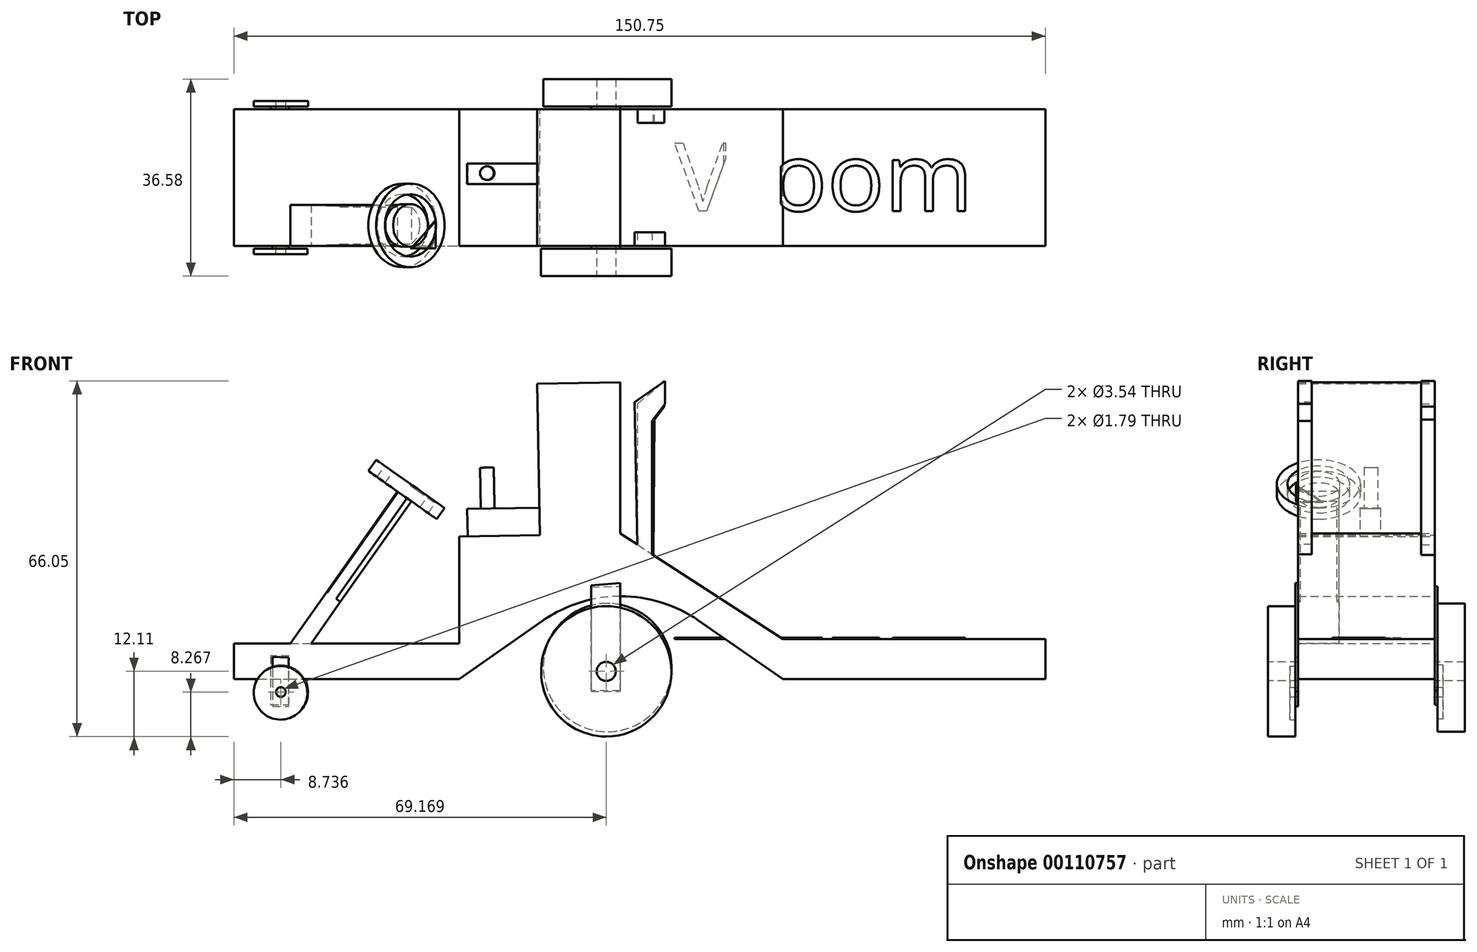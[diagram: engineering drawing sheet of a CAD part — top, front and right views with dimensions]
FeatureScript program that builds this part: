
annotation { "Feature Type Name" : "Feature", "Feature Type Description" : "" }
export const myFeature = defineFeature(function(context is Context, id is Id, definition is map)
    precondition{}
    {
        {
            var Q0;
            Q0=qCreatedBy(makeId("Front.planeOp"),FACE);
            var sketch = newSketch(context, id + "F0", { "sketchPlane" : qUnion([Q0])});
            skLineSegment(sketch, "E0", {"start": v(-71.8, 16.69) * mm, "end": v(-29.94, 16.69) * mm});
            skLineSegment(sketch, "E1", {"start": v(-29.94, 16.69) * mm, "end": v(-14.49, 27.49) * mm});
            skLineSegment(sketch, "E2", {"start": v(14.53, 27.55) * mm, "end": v(30.2, 16.69) * mm});
            skLineSegment(sketch, "E3", {"start": v(30.2, 16.69) * mm, "end": v(78.95, 16.69) * mm});
            skArc(sketch, "E4.filletArc", {"start": v(14.53, 27.55) * mm, "mid": v(0.01, 32.07) * mm, "end": v(-14.49, 27.49) * mm});
            skLineSegment(sketch, "E5", {"start": v(-71.8, 16.69) * mm, "end": v(-71.8, 23.31) * mm});
            skLineSegment(sketch, "E6", {"start": v(-71.8, 23.31) * mm, "end": v(-29.94, 23.31) * mm});
            skLineSegment(sketch, "E7", {"start": v(-29.94, 23.31) * mm, "end": v(0, 43.71) * mm});
            skLineSegment(sketch, "E8", {"start": v(0, 43.71) * mm, "end": v(30.2, 24.1) * mm});
            skLineSegment(sketch, "E9", {"start": v(30.2, 24.1) * mm, "end": v(78.95, 24.1) * mm});
            skLineSegment(sketch, "E10", {"start": v(78.95, 24.1) * mm, "end": v(78.95, 16.69) * mm});
            skLineSegment(sketch, "E11", {"start": v(-29.94, 23.31) * mm, "end": v(-29.94, 43.18) * mm});
            skLineSegment(sketch, "E12", {"start": v(-29.94, 43.18) * mm, "end": v(0, 43.71) * mm});
            skLineSegment(sketch, "E13", {"start": v(-14.97, 43.45) * mm, "end": v(-15.47, 71.53) * mm});
            skLineSegment(sketch, "E14", {"start": v(-15.47, 71.53) * mm, "end": v(0, 71.8) * mm});
            skLineSegment(sketch, "E15", {"start": v(0, 71.8) * mm, "end": v(0, 43.71) * mm});
            skSolve(sketch);
        }
        {
            var Q0;
            Q0 = qSketchRegion(id + "F0", true);
            extrude(context, id + "F1", {"entities" : qUnion([Q0]), "depth" : 25.4 * mm});
        }
        {
            var Q0;
            Q0=makeQuery(id+"F1.opExtrude","CAP_FACE",FACE,{"disambiguationData":[OSD([sQuery(id+"F0.wireOp",EDGE,"E0"),sQuery(id+"F0.wireOp",EDGE,"E1"),sQuery(id+"F0.wireOp",EDGE,"E2"),sQuery(id+"F0.wireOp",EDGE,"E3"),sQuery(id+"F0.wireOp",EDGE,"E4.filletArc"),sQuery(id+"F0.wireOp",EDGE,"E5"),sQuery(id+"F0.wireOp",EDGE,"E6"),sQuery(id+"F0.wireOp",EDGE,"E8"),sQuery(id+"F0.wireOp",EDGE,"E9"),sQuery(id+"F0.wireOp",EDGE,"E10"),sQuery(id+"F0.wireOp",EDGE,"E11"),sQuery(id+"F0.wireOp",EDGE,"E12"),sQuery(id+"F0.wireOp",EDGE,"E13"),sQuery(id+"F0.wireOp",EDGE,"E14"),sQuery(id+"F0.wireOp",EDGE,"E15")])],"isStart":false});
            var sketch = newSketch(context, id + "F2", { "sketchPlane" : qUnion([Q0])});
            skLineSegment(sketch, "E16", {"start": v(-5.44, 34.07) * mm, "end": v(-5.44, 31.47) * mm});
            skLineSegment(sketch, "E17", {"start": v(-5.44, 31.47) * mm, "end": v(-5.44, 14.38) * mm});
            skLineSegment(sketch, "E18", {"start": v(-5.44, 14.38) * mm, "end": v(0, 14.38) * mm});
            skLineSegment(sketch, "E19", {"start": v(0, 14.38) * mm, "end": v(0, 34.55) * mm});
            skLineSegment(sketch, "E20", {"start": v(0, 34.55) * mm, "end": v(-5.44, 34.07) * mm});
            skSolve(sketch);
        }
        {
            var Q0;
            Q0 = qSketchRegion(id + "F2", true);
            extrude(context, id + "F3", {"entities" : qUnion([Q0]), "operationType" : NewBodyOperationType.ADD, "depth" : 0.5 * mm});
        }
        {
            var Q0;
            Q0=makeQuery(id+"F1.opExtrude","CAP_FACE",FACE,{"disambiguationData":[OSD([sQuery(id+"F0.wireOp",EDGE,"E0"),sQuery(id+"F0.wireOp",EDGE,"E1"),sQuery(id+"F0.wireOp",EDGE,"E2"),sQuery(id+"F0.wireOp",EDGE,"E3"),sQuery(id+"F0.wireOp",EDGE,"E4.filletArc"),sQuery(id+"F0.wireOp",EDGE,"E5"),sQuery(id+"F0.wireOp",EDGE,"E6"),sQuery(id+"F0.wireOp",EDGE,"E8"),sQuery(id+"F0.wireOp",EDGE,"E9"),sQuery(id+"F0.wireOp",EDGE,"E10"),sQuery(id+"F0.wireOp",EDGE,"E11"),sQuery(id+"F0.wireOp",EDGE,"E12"),sQuery(id+"F0.wireOp",EDGE,"E13"),sQuery(id+"F0.wireOp",EDGE,"E14"),sQuery(id+"F0.wireOp",EDGE,"E15")])],"isStart":true});
            var sketch = newSketch(context, id + "F4", { "sketchPlane" : qUnion([Q0])});
            skLineSegment(sketch, "E21", {"start": v(0, 33.92) * mm, "end": v(0, 14.54) * mm});
            skLineSegment(sketch, "E22", {"start": v(0, 14.54) * mm, "end": v(5.42, 14.54) * mm});
            skLineSegment(sketch, "E23", {"start": v(5.42, 14.54) * mm, "end": v(5.42, 33.76) * mm});
            skLineSegment(sketch, "E24", {"start": v(5.42, 33.76) * mm, "end": v(0, 33.92) * mm});
            skSolve(sketch);
        }
        {
            var Q0;
            Q0 = qSketchRegion(id + "F4", true);
            extrude(context, id + "F5", {"entities" : qUnion([Q0]), "operationType" : NewBodyOperationType.ADD, "depth" : 0.5 * mm});
        }
        {
            var Q0;
            Q0=makeQuery(id+"F3.opExtrude","CAP_FACE",FACE,{"disambiguationData":[OSD([sQuery(id+"F2.wireOp",EDGE,"E16"),sQuery(id+"F2.wireOp",EDGE,"E17"),sQuery(id+"F2.wireOp",EDGE,"E18"),sQuery(id+"F2.wireOp",EDGE,"E19"),sQuery(id+"F2.wireOp",EDGE,"E20")])],"isStart":false});
            var sketch = newSketch(context, id + "F6", { "sketchPlane" : qUnion([Q0])});
            skCircle(sketch, "E25", {"center": v(-2.63, 18.12) * mm, "radius": 12.1 * mm});
            skSolve(sketch);
        }
        {
            var Q0;
            Q0 = qSketchRegion(id + "F6", true);
            extrude(context, id + "F7", {"entities" : qUnion([Q0]), "operationType" : NewBodyOperationType.ADD, "depth" : 5.08 * mm});
        }
        {
            var Q0;
            Q0=makeQuery(id+"F5.opExtrude","CAP_FACE",FACE,{"disambiguationData":[OSD([sQuery(id+"F4.wireOp",EDGE,"E21"),sQuery(id+"F4.wireOp",EDGE,"E22"),sQuery(id+"F4.wireOp",EDGE,"E23"),sQuery(id+"F4.wireOp",EDGE,"E24")])],"isStart":false});
            var sketch = newSketch(context, id + "F8", { "sketchPlane" : qUnion([Q0])});
            skCircle(sketch, "E26", {"center": v(2.4, 18.83) * mm, "radius": 11.92 * mm});
            skSolve(sketch);
        }
        {
            var Q0;
            Q0 = qSketchRegion(id + "F8", true);
            extrude(context, id + "F9", {"entities" : qUnion([Q0]), "operationType" : NewBodyOperationType.ADD, "depth" : 5.08 * mm});
        }
        {
            var Q0;
            Q0=makeQuery(id+"F1.opExtrude","CAP_FACE",FACE,{"disambiguationData":[OSD([sQuery(id+"F0.wireOp",EDGE,"E0"),sQuery(id+"F0.wireOp",EDGE,"E1"),sQuery(id+"F0.wireOp",EDGE,"E2"),sQuery(id+"F0.wireOp",EDGE,"E3"),sQuery(id+"F0.wireOp",EDGE,"E4.filletArc"),sQuery(id+"F0.wireOp",EDGE,"E5"),sQuery(id+"F0.wireOp",EDGE,"E6"),sQuery(id+"F0.wireOp",EDGE,"E8"),sQuery(id+"F0.wireOp",EDGE,"E9"),sQuery(id+"F0.wireOp",EDGE,"E10"),sQuery(id+"F0.wireOp",EDGE,"E11"),sQuery(id+"F0.wireOp",EDGE,"E12"),sQuery(id+"F0.wireOp",EDGE,"E13"),sQuery(id+"F0.wireOp",EDGE,"E14"),sQuery(id+"F0.wireOp",EDGE,"E15")])],"isStart":false});
            var sketch = newSketch(context, id + "F10", { "sketchPlane" : qUnion([Q0])});
            skLineSegment(sketch, "E27", {"start": v(-61.3, 23.31) * mm, "end": v(-41.43, 51.53) * mm});
            skLineSegment(sketch, "E28", {"start": v(-41.43, 51.53) * mm, "end": v(-38.85, 49.72) * mm});
            skLineSegment(sketch, "E29", {"start": v(-38.85, 49.72) * mm, "end": v(-57.45, 23.31) * mm});
            skLineSegment(sketch, "E30", {"start": v(-57.45, 23.31) * mm, "end": v(-61.3, 23.31) * mm});
            skSolve(sketch);
        }
        {
            var Q0;
            Q0 = qSketchRegion(id + "F10", true);
            extrude(context, id + "F11", {"entities" : qUnion([Q0]), "operationType" : NewBodyOperationType.ADD, "oppositeDirection" : true, "depth" : 7.62 * mm});
        }
        {
            var Q0;
            Q0=makeQuery(id+"F11.opExtrude","SWEPT_FACE",FACE,{"disambiguationData":[OSD([sQuery(id+"F10.wireOp",EDGE,"E28")])]});
            var sketch = newSketch(context, id + "F12", { "sketchPlane" : qUnion([Q0])});
            skCircle(sketch, "E31", {"center": v(-62.38, -21.6) * mm, "radius": 7.77 * mm});
            skPoint(sketch, "E31.centerSnap0", {"position": v(-60.4, -21.6) * mm});
            skSolve(sketch);
        }
        {
            var Q0;
            Q0 = qSketchRegion(id + "F12", true);
            extrude(context, id + "F13", {"entities" : qUnion([Q0]), "operationType" : NewBodyOperationType.ADD, "depth" : 2.54 * mm});
        }
        {
            var Q0;
            Q0=makeQuery(id+"F13.opExtrude","CAP_FACE",FACE,{"disambiguationData":[OSD([sQuery(id+"F12.wireOp",EDGE,"E31")])],"isStart":false});
            var sketch = newSketch(context, id + "F14", { "sketchPlane" : qUnion([Q0])});
            skCircle(sketch, "E32", {"center": v(-62.38, -21.6) * mm, "radius": 5.78 * mm});
            skCircle(sketch, "E33", {"center": v(-62.38, -21.6) * mm, "radius": 3.94 * mm});
            skSolve(sketch);
        }
        {
            var Q0;
            Q0 = qSketchRegion(id + "F14", true);
            extrude(context, id + "F15", {"entities" : qUnion([Q0]), "operationType" : NewBodyOperationType.REMOVE, "oppositeDirection" : true, "depth" : 25.4 * mm});
        }
        {
            var Q0;
            {var subQ0=sQuery(id+"F12.wireOp",EDGE,"E31");Q0=makeQuery(id+"F15.boolean.opBoolean","SPLIT",FACE,{"disambiguationData":[TD([makeQuery(id+"F13.opExtrude","SWEPT_FACE",FACE,{"disambiguationData":[OSD([subQ0])]})])],"derivedFrom":makeQuery(id+"F13.opExtrude","CAP_FACE",FACE,{"disambiguationData":[OSD([subQ0])],"isStart":false})});}
            var sketch = newSketch(context, id + "F16", { "sketchPlane" : qUnion([Q0])});
            skLineSegment(sketch, "E34", {"start": v(-63.82, -27.19) * mm, "end": v(-60.63, -24.46) * mm});
            skLineSegment(sketch, "E35", {"start": v(-60.63, -24.46) * mm, "end": v(-56.65, -20.78) * mm});
            skLineSegment(sketch, "E36", {"start": v(-56.65, -20.78) * mm, "end": v(-56.65, -25.82) * mm});
            skPoint(sketch, "E36.endSnap0", {"position": v(-62.22, -25.82) * mm});
            skLineSegment(sketch, "E37", {"start": v(-56.65, -25.82) * mm, "end": v(-62.22, -25.82) * mm});
            skSolve(sketch);
        }
        {
            var Q0;
            Q0 = qSketchRegion(id + "F16", true);
            extrude(context, id + "F17", {"entities" : qUnion([Q0]), "oppositeDirection" : true, "depth" : 0.25 * mm});
        }
        {
            var Q0;
            Q0=makeQuery(id+"F1.opExtrude","SWEPT_FACE",FACE,{"disambiguationData":[OSD([sQuery(id+"F0.wireOp",EDGE,"E9")])]});
            var sketch = newSketch(context, id + "F18", { "sketchPlane" : qUnion([Q0])});
            skText(sketch, "E38", { "text": "Vroom", "fontName": "OpenSans-Regular.ttf"});
            const initialGuessF18  = {"E38": [0.01007, -0.0189, 1, 0, 0.0127]};
            skSetInitialGuess(sketch, initialGuessF18);
            skSolve(sketch);
        }
        {
            var Q0;
            Q0 = qSketchRegion(id + "F18", true);
            extrude(context, id + "F19", {"entities" : qUnion([Q0]), "operationType" : NewBodyOperationType.ADD, "depth" : 0.25 * mm});
        }
        {
            var Q0;
            Q0=makeQuery(id+"F11.boolean.opBoolean","MERGE",FACE,{"derivedFrom":[makeQuery(id+"F1.opExtrude","CAP_FACE",FACE,{"disambiguationData":[OSD([sQuery(id+"F0.wireOp",EDGE,"E0"),sQuery(id+"F0.wireOp",EDGE,"E1"),sQuery(id+"F0.wireOp",EDGE,"E2"),sQuery(id+"F0.wireOp",EDGE,"E3"),sQuery(id+"F0.wireOp",EDGE,"E4.filletArc"),sQuery(id+"F0.wireOp",EDGE,"E5"),sQuery(id+"F0.wireOp",EDGE,"E6"),sQuery(id+"F0.wireOp",EDGE,"E8"),sQuery(id+"F0.wireOp",EDGE,"E9"),sQuery(id+"F0.wireOp",EDGE,"E10"),sQuery(id+"F0.wireOp",EDGE,"E11"),sQuery(id+"F0.wireOp",EDGE,"E12"),sQuery(id+"F0.wireOp",EDGE,"E13"),sQuery(id+"F0.wireOp",EDGE,"E14"),sQuery(id+"F0.wireOp",EDGE,"E15")])],"isStart":false}),makeQuery(id+"F11.opExtrude","CAP_FACE",FACE,{"disambiguationData":[OSD([sQuery(id+"F10.wireOp",EDGE,"E27"),sQuery(id+"F10.wireOp",EDGE,"E28"),sQuery(id+"F10.wireOp",EDGE,"E29"),sQuery(id+"F10.wireOp",EDGE,"E30")])],"isStart":true})]});
            var sketch = newSketch(context, id + "F20", { "sketchPlane" : qUnion([Q0])});
            skLineSegment(sketch, "E39", {"start": v(3.12, 41.69) * mm, "end": v(2.65, 68.1) * mm});
            skLineSegment(sketch, "E40", {"start": v(2.65, 68.1) * mm, "end": v(8.26, 72.06) * mm});
            skLineSegment(sketch, "E41", {"start": v(8.26, 72.06) * mm, "end": v(8.26, 67.82) * mm});
            skLineSegment(sketch, "E42", {"start": v(8.26, 67.82) * mm, "end": v(5.88, 64.64) * mm});
            skLineSegment(sketch, "E43", {"start": v(5.88, 64.64) * mm, "end": v(5.88, 39.9) * mm});
            skLineSegment(sketch, "E44", {"start": v(5.88, 39.9) * mm, "end": v(3.12, 41.69) * mm});
            skSolve(sketch);
        }
        {
            var Q0;
            Q0=makeQuery(id+"F1.opExtrude","CAP_FACE",FACE,{"disambiguationData":[OSD([sQuery(id+"F0.wireOp",EDGE,"E0"),sQuery(id+"F0.wireOp",EDGE,"E1"),sQuery(id+"F0.wireOp",EDGE,"E2"),sQuery(id+"F0.wireOp",EDGE,"E3"),sQuery(id+"F0.wireOp",EDGE,"E4.filletArc"),sQuery(id+"F0.wireOp",EDGE,"E5"),sQuery(id+"F0.wireOp",EDGE,"E6"),sQuery(id+"F0.wireOp",EDGE,"E8"),sQuery(id+"F0.wireOp",EDGE,"E9"),sQuery(id+"F0.wireOp",EDGE,"E10"),sQuery(id+"F0.wireOp",EDGE,"E11"),sQuery(id+"F0.wireOp",EDGE,"E12"),sQuery(id+"F0.wireOp",EDGE,"E13"),sQuery(id+"F0.wireOp",EDGE,"E14"),sQuery(id+"F0.wireOp",EDGE,"E15")])],"isStart":true});
            var sketch = newSketch(context, id + "F21", { "sketchPlane" : qUnion([Q0])});
            skLineSegment(sketch, "E45", {"start": v(-6.13, 39.73) * mm, "end": v(-3.23, 41.61) * mm});
            skLineSegment(sketch, "E46", {"start": v(-3.23, 41.61) * mm, "end": v(-3.23, 67.82) * mm});
            skLineSegment(sketch, "E47", {"start": v(-3.23, 67.82) * mm, "end": v(-8.16, 72.06) * mm});
            skLineSegment(sketch, "E48", {"start": v(-8.16, 72.06) * mm, "end": v(-8.16, 67.3) * mm});
            skLineSegment(sketch, "E49", {"start": v(-8.16, 67.3) * mm, "end": v(-6.3, 64.9) * mm});
            skLineSegment(sketch, "E50", {"start": v(-6.3, 64.9) * mm, "end": v(-6.13, 39.73) * mm});
            skSolve(sketch);
        }
        {
            var Q0;
            Q0 = qSketchRegion(id + "F21", true);
            extrude(context, id + "F22", {"entities" : qUnion([Q0]), "operationType" : NewBodyOperationType.ADD, "oppositeDirection" : true, "depth" : 2.54 * mm});
        }
        {
            var Q0;
            Q0 = qSketchRegion(id + "F20", true);
            extrude(context, id + "F23", {"entities" : qUnion([Q0]), "operationType" : NewBodyOperationType.ADD, "oppositeDirection" : true, "depth" : 2.54 * mm});
        }
        {
            var Q0;
            Q0=makeQuery(id+"F1.opExtrude","SWEPT_FACE",FACE,{"disambiguationData":[OSD([sQuery(id+"F0.wireOp",EDGE,"E12")])]});
            var sketch = newSketch(context, id + "F24", { "sketchPlane" : qUnion([Q0])});
            skLineSegment(sketch, "E51", {"start": v(-14.2, -10.09) * mm, "end": v(-22.53, -10.09) * mm});
            skLineSegment(sketch, "E52", {"start": v(-22.53, -13.93) * mm, "end": v(-14.2, -13.93) * mm});
            skLineSegment(sketch, "E53", {"start": v(-14.2, -13.93) * mm, "end": v(-14.2, -10.09) * mm});
            skLineSegment(sketch, "E54", {"start": v(-22.53, -10.09) * mm, "end": v(-27.6, -10.09) * mm});
            skLineSegment(sketch, "E55", {"start": v(-27.6, -10.09) * mm, "end": v(-27.6, -13.93) * mm});
            skLineSegment(sketch, "E56", {"start": v(-27.6, -13.93) * mm, "end": v(-22.53, -13.93) * mm});
            skSolve(sketch);
        }
        {
            var Q0;
            Q0 = qSketchRegion(id + "F24", true);
            extrude(context, id + "F25", {"entities" : qUnion([Q0]), "operationType" : NewBodyOperationType.ADD, "depth" : 5.08 * mm});
        }
        {
            var Q0;
            Q0=makeQuery(id+"F25.opExtrude","CAP_FACE",FACE,{"disambiguationData":[OSD([sQuery(id+"F24.wireOp",EDGE,"E51"),sQuery(id+"F24.wireOp",EDGE,"E52"),sQuery(id+"F24.wireOp",EDGE,"E53"),sQuery(id+"F24.wireOp",EDGE,"E54"),sQuery(id+"F24.wireOp",EDGE,"E55"),sQuery(id+"F24.wireOp",EDGE,"E56")])],"isStart":false});
            var sketch = newSketch(context, id + "F26", { "sketchPlane" : qUnion([Q0])});
            skCircle(sketch, "E57", {"center": v(-23.8, -11.89) * mm, "radius": 1.27 * mm});
            skSolve(sketch);
        }
        {
            var Q0;
            Q0 = qSketchRegion(id + "F26", true);
            extrude(context, id + "F27", {"entities" : qUnion([Q0]), "operationType" : NewBodyOperationType.ADD, "depth" : 7.62 * mm});
        }
        {
            var Q0;
            Q0=makeQuery(id+"F7.opExtrude","CAP_FACE",FACE,{"disambiguationData":[OSD([sQuery(id+"F6.wireOp",EDGE,"E25")])],"isStart":false});
            var sketch = newSketch(context, id + "F28", { "sketchPlane" : qUnion([Q0])});
            skCircle(sketch, "E58", {"center": v(-2.63, 18.12) * mm, "radius": 1.77 * mm});
            skSolve(sketch);
        }
        {
            var Q0;
            Q0 = qSketchRegion(id + "F28", true);
            extrude(context, id + "F29", {"entities" : qUnion([Q0]), "operationType" : NewBodyOperationType.REMOVE, "endBound" : BoundingType.THROUGH_ALL, "oppositeDirection" : true, "depth" : 25.4 * mm});
        }
        {
            var Q0;
            Q0=makeQuery(id+"F23.boolean.opBoolean","MERGE",FACE,{"derivedFrom":[makeQuery(id+"F11.boolean.opBoolean","MERGE",FACE,{"derivedFrom":[makeQuery(id+"F1.opExtrude","CAP_FACE",FACE,{"disambiguationData":[OSD([sQuery(id+"F0.wireOp",EDGE,"E0"),sQuery(id+"F0.wireOp",EDGE,"E1"),sQuery(id+"F0.wireOp",EDGE,"E2"),sQuery(id+"F0.wireOp",EDGE,"E3"),sQuery(id+"F0.wireOp",EDGE,"E4.filletArc"),sQuery(id+"F0.wireOp",EDGE,"E5"),sQuery(id+"F0.wireOp",EDGE,"E6"),sQuery(id+"F0.wireOp",EDGE,"E8"),sQuery(id+"F0.wireOp",EDGE,"E9"),sQuery(id+"F0.wireOp",EDGE,"E10"),sQuery(id+"F0.wireOp",EDGE,"E11"),sQuery(id+"F0.wireOp",EDGE,"E12"),sQuery(id+"F0.wireOp",EDGE,"E13"),sQuery(id+"F0.wireOp",EDGE,"E14"),sQuery(id+"F0.wireOp",EDGE,"E15")])],"isStart":false}),makeQuery(id+"F11.opExtrude","CAP_FACE",FACE,{"disambiguationData":[OSD([sQuery(id+"F10.wireOp",EDGE,"E27"),sQuery(id+"F10.wireOp",EDGE,"E28"),sQuery(id+"F10.wireOp",EDGE,"E29"),sQuery(id+"F10.wireOp",EDGE,"E30")])],"isStart":true})]}),makeQuery(id+"F23.opExtrude","CAP_FACE",FACE,{"disambiguationData":[OSD([sQuery(id+"F20.wireOp",EDGE,"E39"),sQuery(id+"F20.wireOp",EDGE,"E40"),sQuery(id+"F20.wireOp",EDGE,"E41"),sQuery(id+"F20.wireOp",EDGE,"E42"),sQuery(id+"F20.wireOp",EDGE,"E43"),sQuery(id+"F20.wireOp",EDGE,"E44")])],"isStart":true})]});
            var sketch = newSketch(context, id + "F30", { "sketchPlane" : qUnion([Q0])});
            skLineSegment(sketch, "E59", {"start": v(-64.61, 20.83) * mm, "end": v(-64.61, 11.62) * mm});
            skLineSegment(sketch, "E60", {"start": v(-64.61, 11.62) * mm, "end": v(-61.64, 11.62) * mm});
            skLineSegment(sketch, "E61", {"start": v(-61.64, 11.62) * mm, "end": v(-61.64, 20.69) * mm});
            skLineSegment(sketch, "E62", {"start": v(-61.64, 20.69) * mm, "end": v(-64.61, 20.83) * mm});
            skSolve(sketch);
        }
        {
            var Q0;
            Q0=makeQuery(id+"F22.boolean.opBoolean","MERGE",FACE,{"derivedFrom":[makeQuery(id+"F1.opExtrude","CAP_FACE",FACE,{"disambiguationData":[OSD([sQuery(id+"F0.wireOp",EDGE,"E0"),sQuery(id+"F0.wireOp",EDGE,"E1"),sQuery(id+"F0.wireOp",EDGE,"E2"),sQuery(id+"F0.wireOp",EDGE,"E3"),sQuery(id+"F0.wireOp",EDGE,"E4.filletArc"),sQuery(id+"F0.wireOp",EDGE,"E5"),sQuery(id+"F0.wireOp",EDGE,"E6"),sQuery(id+"F0.wireOp",EDGE,"E8"),sQuery(id+"F0.wireOp",EDGE,"E9"),sQuery(id+"F0.wireOp",EDGE,"E10"),sQuery(id+"F0.wireOp",EDGE,"E11"),sQuery(id+"F0.wireOp",EDGE,"E12"),sQuery(id+"F0.wireOp",EDGE,"E13"),sQuery(id+"F0.wireOp",EDGE,"E14"),sQuery(id+"F0.wireOp",EDGE,"E15")])],"isStart":true}),makeQuery(id+"F22.opExtrude","CAP_FACE",FACE,{"disambiguationData":[OSD([sQuery(id+"F21.wireOp",EDGE,"E45"),sQuery(id+"F21.wireOp",EDGE,"E46"),sQuery(id+"F21.wireOp",EDGE,"E47"),sQuery(id+"F21.wireOp",EDGE,"E48"),sQuery(id+"F21.wireOp",EDGE,"E49"),sQuery(id+"F21.wireOp",EDGE,"E50")])],"isStart":true})]});
            var sketch = newSketch(context, id + "F31", { "sketchPlane" : qUnion([Q0])});
            skLineSegment(sketch, "E63", {"start": v(61.55, 20.98) * mm, "end": v(64.97, 20.98) * mm});
            skLineSegment(sketch, "E64", {"start": v(64.97, 20.98) * mm, "end": v(64.97, 11.91) * mm});
            skLineSegment(sketch, "E65", {"start": v(64.97, 11.91) * mm, "end": v(61.55, 11.91) * mm});
            skLineSegment(sketch, "E66", {"start": v(61.55, 11.91) * mm, "end": v(61.55, 20.98) * mm});
            skSolve(sketch);
        }
        {
            var Q0;
            Q0 = qSketchRegion(id + "F31", true);
            extrude(context, id + "F32", {"entities" : qUnion([Q0]), "operationType" : NewBodyOperationType.ADD, "depth" : 0.5 * mm});
        }
        {
            var Q0;
            Q0 = qSketchRegion(id + "F30", true);
            extrude(context, id + "F33", {"entities" : qUnion([Q0]), "operationType" : NewBodyOperationType.ADD, "depth" : 0.5 * mm});
        }
        {
            var Q0;
            Q0=makeQuery(id+"F33.opExtrude","CAP_FACE",FACE,{"disambiguationData":[OSD([sQuery(id+"F30.wireOp",EDGE,"E59"),sQuery(id+"F30.wireOp",EDGE,"E60"),sQuery(id+"F30.wireOp",EDGE,"E61"),sQuery(id+"F30.wireOp",EDGE,"E62")])],"isStart":false});
            var sketch = newSketch(context, id + "F34", { "sketchPlane" : qUnion([Q0])});
            skCircle(sketch, "E67", {"center": v(-63.13, 14.13) * mm, "radius": 4.98 * mm});
            skSolve(sketch);
        }
        {
            var Q0;
            Q0 = qSketchRegion(id + "F34", true);
            extrude(context, id + "F35", {"entities" : qUnion([Q0]), "operationType" : NewBodyOperationType.ADD, "depth" : 1.02 * mm});
        }
        {
            var Q0;
            Q0=makeQuery(id+"F32.opExtrude","CAP_FACE",FACE,{"disambiguationData":[OSD([sQuery(id+"F31.wireOp",EDGE,"E63"),sQuery(id+"F31.wireOp",EDGE,"E64"),sQuery(id+"F31.wireOp",EDGE,"E65"),sQuery(id+"F31.wireOp",EDGE,"E66")])],"isStart":false});
            var sketch = newSketch(context, id + "F36", { "sketchPlane" : qUnion([Q0])});
            skCircle(sketch, "E68", {"center": v(63.06, 14.28) * mm, "radius": 5.03 * mm});
            skSolve(sketch);
        }
        {
            var Q0;
            Q0 = qSketchRegion(id + "F36", true);
            extrude(context, id + "F37", {"entities" : qUnion([Q0]), "operationType" : NewBodyOperationType.ADD, "depth" : 1.02 * mm});
        }
        {
            var Q0;
            Q0=makeQuery(id+"F37.opExtrude","CAP_FACE",FACE,{"disambiguationData":[OSD([sQuery(id+"F36.wireOp",EDGE,"E68")])],"isStart":false});
            var sketch = newSketch(context, id + "F38", { "sketchPlane" : qUnion([Q0])});
            skCircle(sketch, "E69", {"center": v(63.06, 14.28) * mm, "radius": 0.9 * mm});
            skSolve(sketch);
        }
        {
            var Q0;
            Q0 = qSketchRegion(id + "F38", true);
            extrude(context, id + "F39", {"entities" : qUnion([Q0]), "operationType" : NewBodyOperationType.REMOVE, "endBound" : BoundingType.THROUGH_ALL, "oppositeDirection" : true, "depth" : 25.4 * mm});
        }
    });
